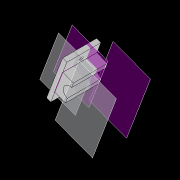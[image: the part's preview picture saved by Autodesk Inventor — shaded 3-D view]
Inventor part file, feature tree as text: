
AUTODESK INVENTOR PART (.ipt)
format: ipt  version: 2021 (Build 250183000, 183)  size: 149,504 bytes
history: native  units: mm
features: plane x5, sketch x5, reference x5, extrude x4, other x4, hole x1
ambient origin geometry x8: Origin, YZ Plane, XZ Plane, XY Plane, X Axis, Y Axis, Z Axis, Center Point
bodies: Solid1 (feature_tree), Solid2 (feature_tree), Solid3 (feature_tree)
feature tree (24):
  plane  "Work Plane1"
  sketch  "Sketch1"  dims[d1=180.0deg d2=50.0mm]
  plane  "Work Plane2"
  extrude  "Extrusion1"  Depth=50.0mm
  plane  "Work Plane3"
  extrude  "Extrusion2"  Depth=50.0mm
  plane  "Work Plane5"
  plane  "Work Plane6"
  extrude  "Extrusion3"  TaperAngle=0.0deg  [1 undecoded]
  extrude  "Extrusion4"  [1 undecoded]
  hole  "Hole1"  [1 undecoded]
  reference  "Reference1"
  sketch  "Sketch2"  dims[d3=100.0mm d4=50.0mm]
  reference  "Reference2"
  reference  "Reference3"
  reference  "Reference4"
  reference  "Reference5"
  sketch  "Sketch3"  dims[d5=10.0mm d6=0.0mm d7=0.0mm]
  sketch  "Sketch4"  dims[d8=20.0mm d9=0.0mm d12=-45.0mm]
  sketch  "Sketch5"  dims[d13=-45.0mm d14=5.0mm d15=100.0mm d16=11.0mm d17=26.9875mm d18=20.0mm d19=0.0mm d20=30.0mm d21=27.2875mm d22=10.0mm d23=0.0mm d24=0.0mm d25=10.0mm d26=6.0mm d27=4.0mm d28=2.0mm d29=90.0deg d30=10.0mm d31=20.594885mm]
  other  "Subensamble_mesa.iam"
  other  "Tubo-2_1_8:1"
  other  "Base soporte tubos:2"
  other  "Eje roscado base soporte tubo:1"
note: 3 required parameter values undecoded (feature->parameter linkage not recoverable at this tier; creation-order binding heuristic only, values carry confidence <= 0.55)
